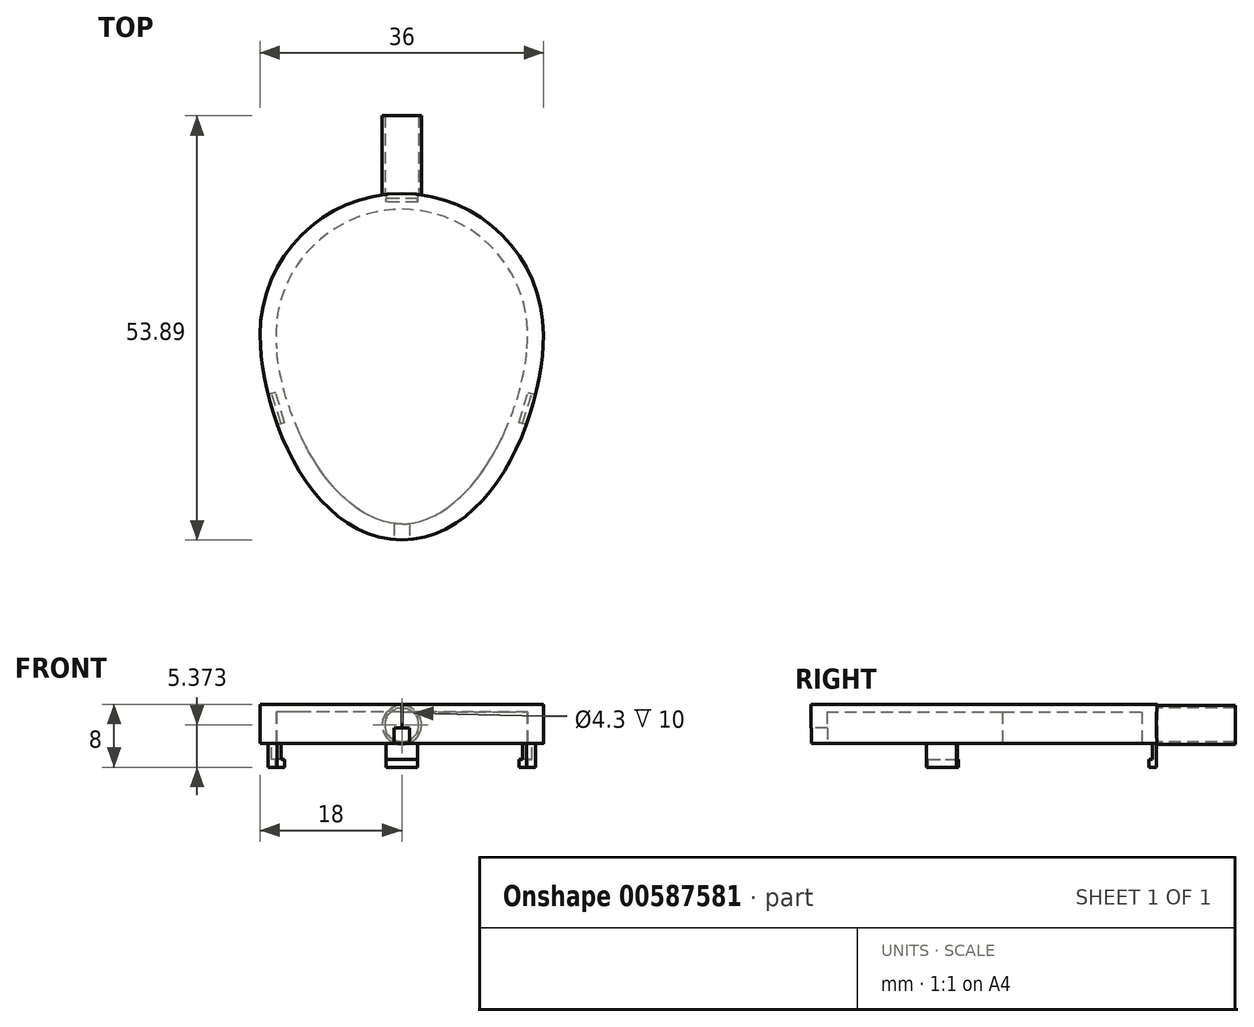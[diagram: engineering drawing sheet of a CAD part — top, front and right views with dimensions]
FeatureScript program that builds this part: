
annotation { "Feature Type Name" : "Feature", "Feature Type Description" : "" }
export const myFeature = defineFeature(function(context is Context, id is Id, definition is map)
    precondition{}
    {
        {
            var Q0;
            Q0=qCreatedBy(makeId("Top.planeOp"),FACE);
            var sketch = newSketch(context, id + "F0", { "sketchPlane" : qUnion([Q0])});
            skCircle(sketch, "E0", {"center": v(0, 0) * mm, "radius": 16 * mm});
            skCircle(sketch, "E1", {"center": v(0, 0) * mm, "radius": 18 * mm});
            skLineSegment(sketch, "E2", {"start": v(0, 0) * mm, "end": v(0, -26) * mm});
            skFitSpline(sketch, "E3", {"points": [v(0, -26) * mm, v(18, 0) * mm], "startDerivative": vector(35.3, 0.42) * mm, "endDerivative": vector(-0.1, 28.78) * mm});
            skLineSegment(sketch, "E4", {"start": v(0, 0) * mm, "end": v(18, 0) * mm});
            skFitSpline(sketch, "E5.MirrorCS", {"points": [v(0, -26) * mm, v(-18, 0) * mm], "startDerivative": vector(-35.3, 0.42) * mm, "endDerivative": vector(0.1, 28.78) * mm});
            skPoint(sketch, "E6", {"position": v(0, -24) * mm});
            skFitSpline(sketch, "E7", {"points": [v(0, -24) * mm, v(16, 0) * mm], "startDerivative": vector(27.48, 0.89) * mm, "endDerivative": vector(0.5, 29.31) * mm});
            skFitSpline(sketch, "E8.MirrorCS", {"points": [v(0, -24) * mm, v(-16, 0) * mm], "startDerivative": vector(-27.48, 0.89) * mm, "endDerivative": vector(-0.5, 29.31) * mm});
            skSolve(sketch);
        }
        {
            var Q0;
            Q0 = qSketchRegion(id + "F0", true);
            extrude(context, id + "F1", {"entities" : qUnion([Q0]), "depth" : 5 * mm, "offsetDistance" : 25 * mm});
        }
        {
            var Q0;
            Q0=makeQuery(id+"F1.opExtrude","CAP_FACE",FACE,{"disambiguationData":[OSD([sQuery(id+"F0.wireOp",EDGE,"E0"),sQuery(id+"F0.wireOp",EDGE,"E1"),sQuery(id+"F0.wireOp",EDGE,"E3"),sQuery(id+"F0.wireOp",EDGE,"E5.MirrorCS"),sQuery(id+"F0.wireOp",EDGE,"E7"),sQuery(id+"F0.wireOp",EDGE,"E8.MirrorCS")])],"isStart":false});
            var sketch = newSketch(context, id + "F2", { "sketchPlane" : qUnion([Q0])});
            skSolve(sketch);
        }
        {
            var Q0;
            Q0=makeQuery(id+"F2.imprint","IMPRINT",FACE,{"disambiguationData":[TD([[makeQuery(id+"F2.imprint","IMPRINT",EDGE,{"derivedFrom":makeQuery(id+"F1.opExtrude","CAP_EDGE",EDGE,{"disambiguationData":[OSD([sQuery(id+"F0.wireOp",EDGE,"E0")])],"isStart":false})}),1.0]])]});
            extrude(context, id + "F3", {"entities" : qUnion([Q0]), "operationType" : NewBodyOperationType.ADD, "oppositeDirection" : true, "depth" : 1 * mm, "offsetDistance" : 25 * mm});
        }
        {
            var Q0;
            Q0=makeQuery(id+"F1.opExtrude","CAP_FACE",FACE,{"disambiguationData":[OSD([sQuery(id+"F0.wireOp",EDGE,"E0"),sQuery(id+"F0.wireOp",EDGE,"E1"),sQuery(id+"F0.wireOp",EDGE,"E3"),sQuery(id+"F0.wireOp",EDGE,"E5.MirrorCS"),sQuery(id+"F0.wireOp",EDGE,"E7"),sQuery(id+"F0.wireOp",EDGE,"E8.MirrorCS")])],"isStart":true});
            var sketch = newSketch(context, id + "F4", { "sketchPlane" : qUnion([Q0])});
            skLineSegment(sketch, "E9.bottom", {"start": v(2, -17.89) * mm, "end": v(-2, -17.89) * mm});
            skLineSegment(sketch, "E9.top", {"start": v(2, -17.39) * mm, "end": v(-2, -17.39) * mm});
            skLineSegment(sketch, "E9.left", {"start": v(2, -17.89) * mm, "end": v(2, -17.39) * mm});
            skLineSegment(sketch, "E9.right", {"start": v(-2, -17.89) * mm, "end": v(-2, -17.39) * mm});
            skLineSegment(sketch, "E10", {"start": v(15.82, 11.36) * mm, "end": v(15.35, 11.22) * mm});
            skLineSegment(sketch, "E11", {"start": v(15.35, 11.22) * mm, "end": v(16.52, 7.4) * mm});
            skLineSegment(sketch, "E12", {"start": v(16.52, 7.4) * mm, "end": v(17, 7.54) * mm});
            skLineSegment(sketch, "E13", {"start": v(17, 7.54) * mm, "end": v(15.82, 11.36) * mm});
            skLineSegment(sketch, "E14", {"start": v(0, 0) * mm, "end": v(0, 17.55) * mm});
            skLineSegment(sketch, "E15.MirrorCS", {"start": v(-17, 7.54) * mm, "end": v(-15.82, 11.36) * mm});
            skLineSegment(sketch, "E16.MirrorCS", {"start": v(-16.52, 7.4) * mm, "end": v(-17, 7.54) * mm});
            skLineSegment(sketch, "E17.MirrorCS", {"start": v(-15.35, 11.22) * mm, "end": v(-16.52, 7.4) * mm});
            skLineSegment(sketch, "E18.MirrorCS", {"start": v(-15.82, 11.36) * mm, "end": v(-15.35, 11.22) * mm});
            skSolve(sketch);
        }
        {
            var Q0;
            Q0 = qSketchRegion(id + "F4", true);
            extrude(context, id + "F5", {"entities" : qUnion([Q0]), "operationType" : NewBodyOperationType.ADD, "depth" : 3 * mm, "offsetDistance" : 25 * mm});
        }
        {
            var Q0;
            Q0=makeQuery(id+"F5.opExtrude","SWEPT_FACE",FACE,{"disambiguationData":[OSD([sQuery(id+"F4.wireOp",EDGE,"E17.MirrorCS")])]});
            var sketch = newSketch(context, id + "F6", { "sketchPlane" : qUnion([Q0])});
            skLineSegment(sketch, "E19", {"start": v(-6.2, -2) * mm, "end": v(-2.2, -2) * mm});
            skSolve(sketch);
        }
        {
            var Q0;
            Q0 = qSketchRegion(id + "F6", true);
            var Q1;
            {var subQ0=sQuery(id+"F6.wireOp",EDGE,"E19");Q1=makeQuery(id+"F6.imprint","IMPRINT",FACE,{"disambiguationData":[TD([[makeQuery(id+"F6.imprint","IMPRINT",EDGE,{"derivedFrom":subQ0}),-1.0]])]});}
            extrude(context, id + "F7", {"entities" : qUnion([Q0, Q1]), "operationType" : NewBodyOperationType.ADD, "depth" : 0.5 * mm, "offsetDistance" : 25 * mm});
        }
        {
            var Q0;
            Q0=makeQuery(id+"F5.opExtrude","SWEPT_FACE",FACE,{"disambiguationData":[OSD([sQuery(id+"F4.wireOp",EDGE,"E11")])]});
            var sketch = newSketch(context, id + "F8", { "sketchPlane" : qUnion([Q0])});
            skLineSegment(sketch, "E20", {"start": v(2.2, -2) * mm, "end": v(6.2, -2) * mm});
            skSolve(sketch);
        }
        {
            var Q0;
            Q0 = qSketchRegion(id + "F8", true);
            var Q1;
            {var subQ0=sQuery(id+"F8.wireOp",EDGE,"E20");Q1=makeQuery(id+"F8.imprint","IMPRINT",FACE,{"disambiguationData":[TD([[makeQuery(id+"F8.imprint","IMPRINT",EDGE,{"derivedFrom":subQ0}),-1.0]])]});}
            extrude(context, id + "F9", {"entities" : qUnion([Q0, Q1]), "operationType" : NewBodyOperationType.ADD, "depth" : 0.5 * mm, "offsetDistance" : 25 * mm});
        }
        {
            var Q0;
            Q0=makeQuery(id+"F5.opExtrude","SWEPT_FACE",FACE,{"disambiguationData":[OSD([sQuery(id+"F4.wireOp",EDGE,"E9.top")])]});
            var sketch = newSketch(context, id + "F10", { "sketchPlane" : qUnion([Q0])});
            skLineSegment(sketch, "E21", {"start": v(2, -2) * mm, "end": v(-2, -2) * mm});
            skSolve(sketch);
        }
        {
            var Q0;
            Q0 = qSketchRegion(id + "F10", true);
            var Q1;
            {var subQ0=sQuery(id+"F10.wireOp",EDGE,"E21");Q1=makeQuery(id+"F10.imprint","IMPRINT",FACE,{"disambiguationData":[TD([[makeQuery(id+"F10.imprint","IMPRINT",EDGE,{"derivedFrom":subQ0}),1.0]])]});}
            extrude(context, id + "F11", {"entities" : qUnion([Q0, Q1]), "operationType" : NewBodyOperationType.ADD, "depth" : 0.5 * mm, "offsetDistance" : 25 * mm});
        }
        {
            var Q0;
            {var subQ0=sQuery(id+"F0.wireOp",EDGE,"E7");var subQ1=sQuery(id+"F0.wireOp",EDGE,"E1");var subQ2=sQuery(id+"F0.wireOp",EDGE,"E8.MirrorCS");var subQ3=sQuery(id+"F0.wireOp",EDGE,"E5.MirrorCS");var subQ4=sQuery(id+"F0.wireOp",EDGE,"E0");var subQ5=sQuery(id+"F0.wireOp",EDGE,"E3");var subQ6=makeQuery(id+"F1.opExtrude","CAP_FACE",FACE,{"disambiguationData":[OSD([subQ4,subQ1,subQ5,subQ3,subQ0,subQ2])],"isStart":true});Q0=makeQuery(id+"F5.boolean.opBoolean","SPLIT",FACE,{"disambiguationData":[TD([makeQuery(id+"F1.opExtrude","SWEPT_FACE",FACE,{"disambiguationData":[OSD([subQ4])]}),subQ6,makeQuery(id+"F1.opExtrude","SWEPT_FACE",FACE,{"disambiguationData":[OSD([subQ1])]}),makeQuery(id+"F1.opExtrude","SWEPT_FACE",FACE,{"disambiguationData":[OSD([subQ5])]}),makeQuery(id+"F1.opExtrude","SWEPT_FACE",FACE,{"disambiguationData":[OSD([subQ3])]}),makeQuery(id+"F1.opExtrude","SWEPT_FACE",FACE,{"disambiguationData":[OSD([subQ0])]}),makeQuery(id+"F1.opExtrude","SWEPT_FACE",FACE,{"disambiguationData":[OSD([subQ2])]}),makeQuery(id+"F5.opExtrude","SWEPT_FACE",FACE,{"disambiguationData":[OSD([sQuery(id+"F4.wireOp",EDGE,"E9.bottom")])]}),makeQuery(id+"F5.opExtrude","SWEPT_FACE",FACE,{"disambiguationData":[OSD([sQuery(id+"F4.wireOp",EDGE,"E9.top")])]}),makeQuery(id+"F5.opExtrude","SWEPT_FACE",FACE,{"disambiguationData":[OSD([sQuery(id+"F4.wireOp",EDGE,"E9.left")])]}),makeQuery(id+"F5.opExtrude","SWEPT_FACE",FACE,{"disambiguationData":[OSD([sQuery(id+"F4.wireOp",EDGE,"E9.right")])]}),makeQuery(id+"F5.opExtrude","SWEPT_FACE",FACE,{"disambiguationData":[OSD([sQuery(id+"F4.wireOp",EDGE,"E10")])]}),makeQuery(id+"F5.opExtrude","SWEPT_FACE",FACE,{"disambiguationData":[OSD([sQuery(id+"F4.wireOp",EDGE,"E11")])]}),makeQuery(id+"F5.opExtrude","SWEPT_FACE",FACE,{"disambiguationData":[OSD([sQuery(id+"F4.wireOp",EDGE,"E12")])]}),makeQuery(id+"F5.opExtrude","SWEPT_FACE",FACE,{"disambiguationData":[OSD([sQuery(id+"F4.wireOp",EDGE,"E13")])]}),makeQuery(id+"F5.opExtrude","SWEPT_FACE",FACE,{"disambiguationData":[OSD([sQuery(id+"F4.wireOp",EDGE,"E15.MirrorCS")])]}),makeQuery(id+"F5.opExtrude","SWEPT_FACE",FACE,{"disambiguationData":[OSD([sQuery(id+"F4.wireOp",EDGE,"E16.MirrorCS")])]}),makeQuery(id+"F5.opExtrude","SWEPT_FACE",FACE,{"disambiguationData":[OSD([sQuery(id+"F4.wireOp",EDGE,"E17.MirrorCS")])]}),makeQuery(id+"F5.opExtrude","SWEPT_FACE",FACE,{"disambiguationData":[OSD([sQuery(id+"F4.wireOp",EDGE,"E18.MirrorCS")])]})])],"derivedFrom":subQ6});}
            var sketch = newSketch(context, id + "F12", { "sketchPlane" : qUnion([Q0])});
            skLineSegment(sketch, "E22", {"start": v(1, 23.91) * mm, "end": v(1, 25.95) * mm});
            skLineSegment(sketch, "E23", {"start": v(-1, 23.91) * mm, "end": v(-1, 25.95) * mm});
            skSolve(sketch);
        }
        {
            var Q0;
            {var subQ6=sQuery(id+"F12.wireOp",EDGE,"E22");Q0=makeQuery(id+"F12.imprint","IMPRINT",FACE,{"disambiguationData":[TD([[makeQuery(id+"F12.imprint","IMPRINT",EDGE,{"derivedFrom":subQ6}),1.0]])]});}
            extrude(context, id + "F13", {"entities" : qUnion([Q0]), "operationType" : NewBodyOperationType.REMOVE, "oppositeDirection" : true, "depth" : 2 * mm, "offsetDistance" : 25 * mm});
        }
        {
            var Q0;
            Q0=makeQuery(id+"F5.opExtrude","SWEPT_FACE",FACE,{"disambiguationData":[OSD([sQuery(id+"F4.wireOp",EDGE,"E9.bottom")])]});
            var sketch = newSketch(context, id + "F14", { "sketchPlane" : qUnion([Q0])});
            skCircle(sketch, "E24", {"center": v(0, 2.37) * mm, "radius": 2.5 * mm});
            skCircle(sketch, "E25", {"center": v(0, 2.37) * mm, "radius": 2.15 * mm});
            skLineSegment(sketch, "E26", {"start": v(0, -3) * mm, "end": v(0, 8.24) * mm});
            skPoint(sketch, "E27", {"position": v(0, 2.62) * mm});
            skSolve(sketch);
        }
        {
            var Q0;
            Q0 = qSketchRegion(id + "F14", true);
            extrude(context, id + "F15", {"entities" : qUnion([Q0]), "operationType" : NewBodyOperationType.ADD, "depth" : 10 * mm, "offsetDistance" : 25 * mm});
        }
    });
